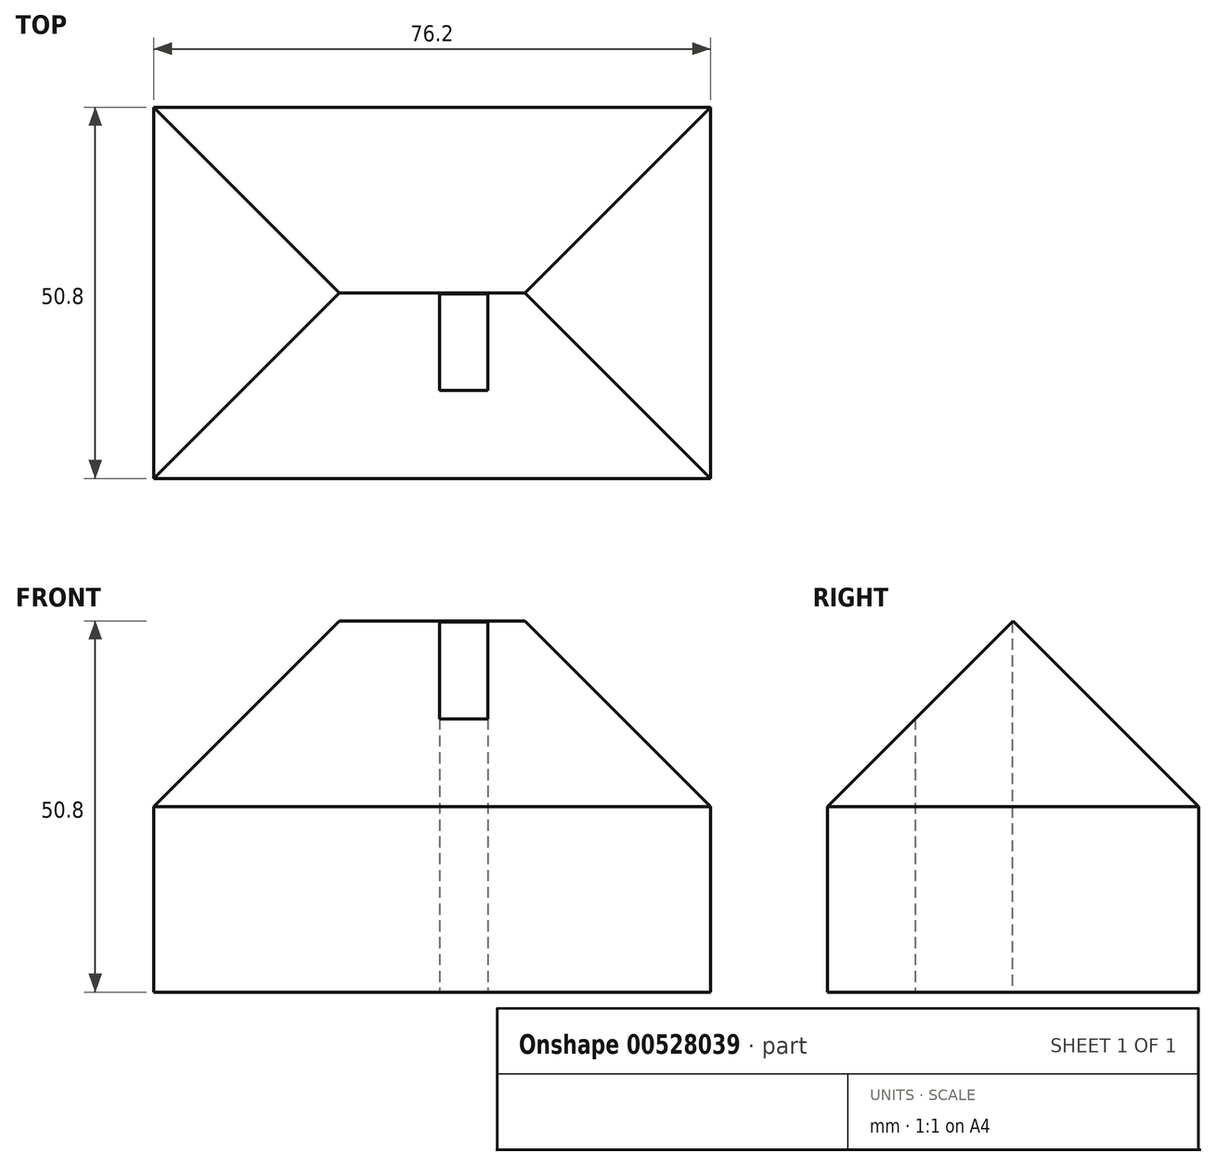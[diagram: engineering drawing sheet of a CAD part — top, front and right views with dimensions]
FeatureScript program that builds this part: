
annotation { "Feature Type Name" : "Feature", "Feature Type Description" : "" }
export const myFeature = defineFeature(function(context is Context, id is Id, definition is map)
    precondition{}
    {
        {
            var Q0;
            Q0=qCreatedBy(makeId("Top.planeOp"),FACE);
            var sketch = newSketch(context, id + "F0", { "sketchPlane" : qUnion([Q0])});
            skLineSegment(sketch, "E0.bottom", {"start": v(0, 0) * mm, "end": v(76.2, 0) * mm});
            skLineSegment(sketch, "E0.top", {"start": v(0, 50.8) * mm, "end": v(76.2, 50.8) * mm});
            skLineSegment(sketch, "E0.left", {"start": v(0, 0) * mm, "end": v(0, 50.8) * mm});
            skLineSegment(sketch, "E0.right", {"start": v(76.2, 0) * mm, "end": v(76.2, 50.8) * mm});
            skSolve(sketch);
        }
        {
            var Q0;
            Q0=qSketchRegion(id+"F0",true);
            extrude(context, id + "F1", {"entities" : qUnion([Q0]), "depth" : 50.8 * mm});
        }
        {
            var Q0;
            Q0=makeQuery(id+"F1.opExtrude","SWEPT_FACE",FACE,{"disambiguationData":[OSD([sQuery(id+"F0.wireOp",EDGE,"E0.top")])]});
            var sketch = newSketch(context, id + "F2", { "sketchPlane" : qUnion([Q0])});
            skCircle(sketch, "E1", {"center": v(-38.1, 25.4) * mm, "radius": 12.7 * mm});
            skSolve(sketch);
        }
        {
            var Q0;
            Q0=makeQuery(id+"F1.opExtrude","CAP_EDGE",EDGE,{"disambiguationData":[OSD([sQuery(id+"F0.wireOp",EDGE,"E0.left")])],"isStart":false});
            var Q1;
            Q1=makeQuery(id+"F1.opExtrude","CAP_EDGE",EDGE,{"disambiguationData":[OSD([sQuery(id+"F0.wireOp",EDGE,"E0.right")])],"isStart":false});
            var Q2;
            Q2=makeQuery(id+"F1.opExtrude","CAP_EDGE",EDGE,{"disambiguationData":[OSD([sQuery(id+"F0.wireOp",EDGE,"E0.bottom")])],"isStart":false});
            var Q3;
            Q3=makeQuery(id+"F1.opExtrude","CAP_EDGE",EDGE,{"disambiguationData":[OSD([sQuery(id+"F0.wireOp",EDGE,"E0.top")])],"isStart":false});
            chamfer(context, id + "F3", {"entities" : qUnion([Q0, Q1, Q2, Q3]), "width" : 25.4 * mm, "tangentPropagation" : true});
        }
        {
            var Q0;
            Q0=makeQuery(id+"F1.opExtrude","CAP_FACE",FACE,{"disambiguationData":[OSD([sQuery(id+"F0.wireOp",EDGE,"E0.bottom"),sQuery(id+"F0.wireOp",EDGE,"E0.top"),sQuery(id+"F0.wireOp",EDGE,"E0.left"),sQuery(id+"F0.wireOp",EDGE,"E0.right")])],"isStart":true});
            var sketch = newSketch(context, id + "F4", { "sketchPlane" : qUnion([Q0])});
            skLineSegment(sketch, "E2.bottom", {"start": v(39.1, -25.26) * mm, "end": v(45.73, -25.26) * mm});
            skLineSegment(sketch, "E2.top", {"start": v(39.1, -12) * mm, "end": v(45.73, -12) * mm});
            skLineSegment(sketch, "E2.left", {"start": v(39.1, -25.26) * mm, "end": v(39.1, -12) * mm});
            skLineSegment(sketch, "E2.right", {"start": v(45.73, -25.26) * mm, "end": v(45.73, -12) * mm});
            skPoint(sketch, "E2.middle", {"position": v(42.42, -18.63) * mm});
            skSolve(sketch);
        }
        {
            var Q0;
            Q0=qSketchRegion(id+"F4",true);
            extrude(context, id + "F5", {"entities" : qUnion([Q0]), "operationType" : NewBodyOperationType.REMOVE, "endBound" : BoundingType.THROUGH_ALL, "oppositeDirection" : true, "depth" : 25.4 * mm});
        }
    });
